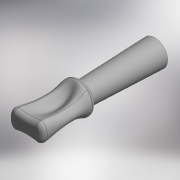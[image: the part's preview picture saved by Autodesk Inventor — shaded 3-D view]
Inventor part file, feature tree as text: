
AUTODESK INVENTOR PART (.ipt)
format: ipt  version: 2018 (Build 220112000, 112)  size: 358,912 bytes
history: native  units: in
note: dims shown in document units (in); Inventor stores cm internally (conversion verified against a paired STEP export)
features: other x5, extrude x3, loft x3, fillet x2, plane x1, sheet_metal_op x1
ambient origin geometry x8: Origin, YZ Plane, XZ Plane, XY Plane, X Axis, Y Axis, Z Axis, Center Point
bodies: Solid1 (feature_tree)
feature tree (15):
  extrude  "Plug"  [1 undecoded]
  extrude  "Extrusion2"  Depth=0.3937in
  plane  "Work Plane1"
  extrude  "Cap"  TaperAngle=0.0deg  [1 undecoded]
  loft  "Handle Loft"
  sheet_metal_op  "Notch"
  fillet  "Fillet1"  Radius=0.0787in
  fillet  "Fillet4"  Radius=0.3937in
  other  "Plug Size"
  other  "Handle End Sketch"
  loft  "Loft Rails"
  loft  "Loft Start"
  other  "Notch Sketch"
  other  "Edges6"
  other  "Edges8"
note: 2 required parameter values undecoded (feature->parameter linkage not recoverable at this tier; creation-order binding heuristic only, values carry confidence <= 0.55)
